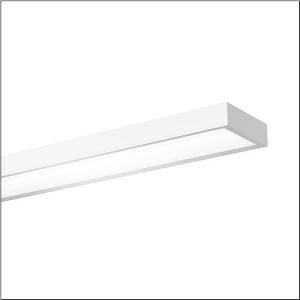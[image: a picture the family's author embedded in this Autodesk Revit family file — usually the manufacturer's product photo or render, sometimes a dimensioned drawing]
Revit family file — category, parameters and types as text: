
# Revit family: sport_31_51hs12dc4eca
name_source: partatom
category: Lighting Fixtures
units: mm (PartAtom-declared; Revit-internal decimal feet)

## family parameters
Cut with Voids When Loaded = No
Host = Face
Light Source = No
Part Type = Normal
Room Calculation Point = No
Round Connector Dimension = Use Diameter
Shared = No

## types (1)
- --- (1 x LED, 11990 lm, 89.4 W, 4000K)
    Apparent Load = 89 VA
    CIE Flux Codes = 65 89 97 100 100
    Color Rendering = 80
    Color Temperature = 4000K
    Default Elevation = 1800 mm
    Description = Sport 31, high bay luminaire, primary light control with reflector, of sheet steel, primary anti-glare with prismatic structure, of PC, primary optical cover: cover panel, of PC, light emission: direct distribution, primary light characteristic: symmetric, installation type: suspended mounting, recessed, surface-mounted, LED, rated luminous flux: 12.000lm, luminous efficacy: 137lm/W, light colour: 840, colour temperature: 4000K, control gear: DALI 2, with terminal, 5-pole, max. 2.5mm², mains connection: 220..240V, AC/DC, 50/60Hz, rated input power: 88W, housing, of sheet steel, traffic white (RAL 9016), length: 1.540mm, width: 315mm, height: 95mm, protection rating (complete): IP20, protection rating (lamp compartment, on room side): IP50, insulation class (complete): insulation class I (protective earthing), certification: CE, ENEC, UKCA, ball protection: ball impact resistant with ceiling mounting or chain suspension, impact resistance: IK08, permissible operating ambient temperature: -20..+35°C, standard: DIN 18032-3, EN 60598-2-22, packaging unit: 1 piece
    Height = 100 mm  [stored 0.328084 ft]
    Lamp = 1 x LED
    Lamp Light Flux = 11990 lm
    Lamp Power = 89.4 W
    Lamp count = 1
    Length = 1500 mm
    Luminous efficacy = 134 lm/W
    Manufacturer = Siteco
    ModVariant = No
    Model = 51HS12DC4ECA
    Mounting Place = Ceiling
    Mounting Type = Pendant
    Number of Poles = 1
    OnlyDefault = Yes
    Power Factor = 1
    Product Name = Sport 31
    Product group = high bay luminaire
    ProductGroupID = 902
    Protection Class = Protection class I
    Protection Degree = IP 20
    RLX_Detail_Level = 1
    RLX_Emergency_Light_Flux = 0 lm
    RLX_Emergency_Type = 0
    RLX_Emergency_Type_DB = No
    RlxData = <blob elided: 22833 chars, md5=7bad3400>
    Socket = socket
    Standby Power = 0 W
    System Light Flux = 11990 lm
    System Power = 89 W
    Type Comments = factory setting: luminous flux: 100 % | dim-lin: 254 | 380 mA
    Type Image = l_1397489.jpg
    URL = http://relux.com
    VarID = @adj_198435
    Voltage = 0 V
    Weight = 0.00 kg
    Width = 315 mm

note: [stored X ft] marks values corroborated as IEEE doubles in the binary element streams (Revit-internal decimal feet)

## geometry (parser evidence)
native form markers: Blend x4, Sweep x11
no freeform markers — native parametric forms only
